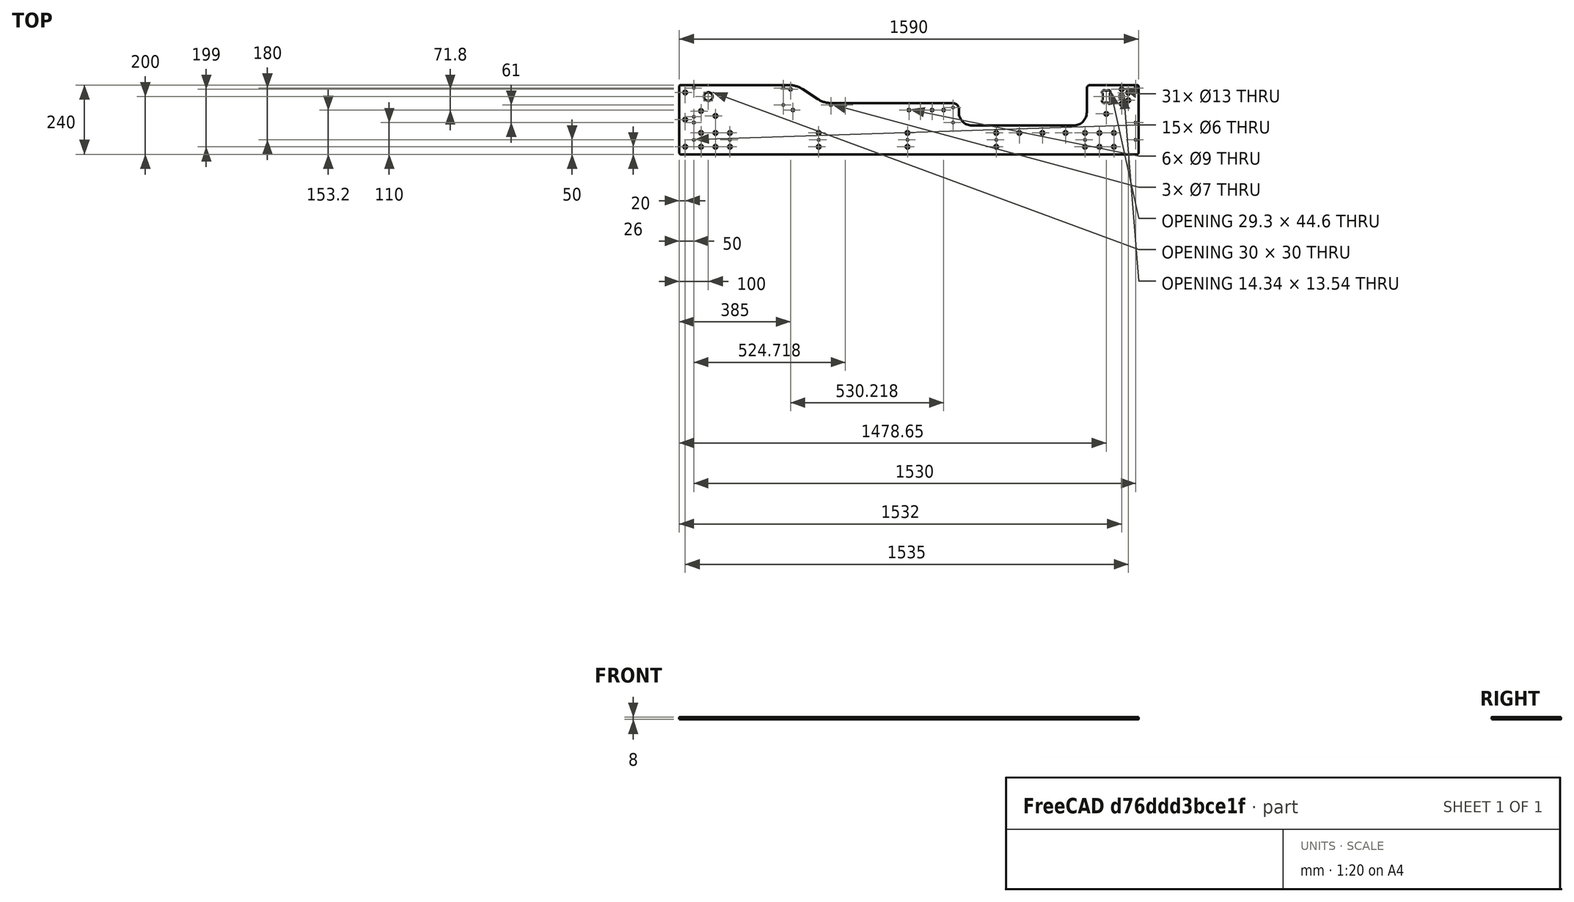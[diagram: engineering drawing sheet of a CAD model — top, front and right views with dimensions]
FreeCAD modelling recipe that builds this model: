
FCSTD DOCUMENT  (FreeCAD 0.19R24267 +99 (Git))
Label: V2 Side mounting plate
License: All rights reserved
LicenseURL: http://en.wikipedia.org/wiki/All_rights_reserved
objects: Sketcher::SketchObject×1, PartDesign::Pad×1, PartDesign::Body×1
note: 4 computed .brp shape members not serialized (recipe doc carries the construction recipe); baked Part::Feature solids carry a one-line shape summary decoded from their .brp

FEATURE [Sketcher::SketchObject] Sketch  label="Profile and holes sketch"
  FullyConstrained = true
  MapMode = 5
  Support = -> [XY_Plane]
  sketch-geometry (196):
    g0: LineSegment StartX=750 StartY=140 StartZ=0 EndX=750 EndY=-100 EndZ=0
    g1: LineSegment StartX=-750 StartY=-100 StartZ=0 EndX=-750 EndY=140 EndZ=0
    g2: ArcOfCircle CenterX=-690 CenterY=100 CenterZ=0 NormalX=0 NormalY=0 NormalZ=1 AngleXU=0 Radius=15 StartAngle=4.71239 EndAngle=7.85398
    g3: LineSegment StartX=223 StartY=0 StartZ=0 EndX=576 EndY=0 EndZ=0
    g4: LineSegment StartX=621 StartY=45 StartZ=0 EndX=621 EndY=128 EndZ=0
    g5: LineSegment StartX=-690 StartY=100 StartZ=0 EndX=60.218 EndY=100 EndZ=0
    g6: LineSegment StartX=60.218 StartY=100 StartZ=0 EndX=60.218 EndY=53.2 EndZ=0
    g7: LineSegment StartX=178 StartY=53.2 StartZ=0 EndX=-750 EndY=53.2 EndZ=0
    g8: LineSegment StartX=-307.5 StartY=-26 StartZ=0 EndX=-307.5 EndY=-74 EndZ=0
    g9: LineSegment StartX=307.5 StartY=-26 StartZ=0 EndX=307.5 EndY=-74 EndZ=0
    g10: LineSegment StartX=715 StartY=-26 StartZ=0 EndX=715 EndY=-74 EndZ=0
    g11: LineSegment StartX=-307.5 StartY=-74 StartZ=0 EndX=0 EndY=-74 EndZ=0
    g12: LineSegment StartX=2.29e-14 StartY=-74 StartZ=0 EndX=307.5 EndY=-74 EndZ=0
    g13: GeomPoint X=2.29e-14 Y=-26 Z=0
    g14: Circle CenterX=-715 CenterY=50 CenterZ=0 NormalX=0 NormalY=0 NormalZ=1 AngleXU=0 Radius=6.5
    g15: Circle CenterX=-665 CenterY=33 CenterZ=0 NormalX=0 NormalY=0 NormalZ=1 AngleXU=0 Radius=6.5
    g16: Circle CenterX=-715 CenterY=-26 CenterZ=0 NormalX=0 NormalY=0 NormalZ=1 AngleXU=0 Radius=6.5
    g17: Circle CenterX=-307.5 CenterY=-26 CenterZ=0 NormalX=0 NormalY=0 NormalZ=1 AngleXU=0 Radius=6.5
    g18: Circle CenterX=-307.5 CenterY=-74 CenterZ=0 NormalX=0 NormalY=0 NormalZ=1 AngleXU=0 Radius=6.5
    g19: Circle CenterX=2.29e-14 CenterY=-74 CenterZ=0 NormalX=0 NormalY=0 NormalZ=1 AngleXU=0 Radius=6.5
    g20: Circle CenterX=2.29e-14 CenterY=-26 CenterZ=0 NormalX=0 NormalY=0 NormalZ=1 AngleXU=0 Radius=6.5
    g21: Circle CenterX=307.5 CenterY=-74 CenterZ=0 NormalX=0 NormalY=0 NormalZ=1 AngleXU=0 Radius=6.5
    g22: Circle CenterX=307.5 CenterY=-26 CenterZ=0 NormalX=0 NormalY=0 NormalZ=1 AngleXU=0 Radius=6.5
    g23: Circle CenterX=715 CenterY=-26 CenterZ=0 NormalX=0 NormalY=0 NormalZ=1 AngleXU=0 Radius=6.5
    g24: Circle CenterX=715 CenterY=-74 CenterZ=0 NormalX=0 NormalY=0 NormalZ=1 AngleXU=0 Radius=6.5
    g25: Circle CenterX=307.5 CenterY=-50 CenterZ=0 NormalX=0 NormalY=0 NormalZ=1 AngleXU=0 Radius=3
    g26: Circle CenterX=-307.5 CenterY=-50 CenterZ=0 NormalX=0 NormalY=0 NormalZ=1 AngleXU=0 Radius=3
    g27: LineSegment StartX=-786 StartY=140 StartZ=0 EndX=-412 EndY=140 EndZ=0
    g28: LineSegment StartX=-362.763 StartY=125.338 StartZ=0 EndX=-311.237 EndY=91.6625 EndZ=0
    g29: LineSegment StartX=-262 StartY=77 StartZ=0 EndX=158 EndY=77 EndZ=0
    g30: ArcOfCircle CenterX=-412 CenterY=50 CenterZ=0 NormalX=0 NormalY=0 NormalZ=1 AngleXU=0 Radius=90 StartAngle=0.991931 EndAngle=1.5708
    g31: ArcOfCircle CenterX=-262 CenterY=167 CenterZ=0 NormalX=0 NormalY=0 NormalZ=1 AngleXU=0 Radius=90 StartAngle=4.13352 EndAngle=4.71239
    g32: LineSegment StartX=633 StartY=140 StartZ=0 EndX=796 EndY=140 EndZ=0
    g33: ArcOfCircle CenterX=158 CenterY=57 CenterZ=0 NormalX=0 NormalY=0 NormalZ=1 AngleXU=0 Radius=20 StartAngle=0 EndAngle=1.5708
    g34: LineSegment StartX=-715 StartY=-26 StartZ=0 EndX=-715 EndY=-74 EndZ=0
    g35: Circle CenterX=-715 CenterY=-74 CenterZ=0 NormalX=0 NormalY=0 NormalZ=1 AngleXU=0 Radius=6.5
    g36: LineSegment StartX=688.244 StartY=120.3 StartZ=0 EndX=689.056 EndY=120.3 EndZ=0
    g37: LineSegment StartX=701.3 StartY=108.056 StartZ=0 EndX=701.3 EndY=91.9438 EndZ=0
    g38: LineSegment StartX=689.056 StartY=79.7 StartZ=0 EndX=688.244 EndY=79.7 EndZ=0
    g39: LineSegment StartX=676 StartY=91.9438 StartZ=0 EndX=676 EndY=108.056 EndZ=0
    g40: ArcOfCircle CenterX=680.95 CenterY=115.35 CenterZ=0 NormalX=0 NormalY=0 NormalZ=1 AngleXU=0 Radius=7 StartAngle=1.02277 EndAngle=3.68962
    g41: ArcOfCircle CenterX=680.95 CenterY=84.6497 CenterZ=0 NormalX=0 NormalY=0 NormalZ=1 AngleXU=0 Radius=7 StartAngle=2.59356 EndAngle=5.26042
    g42: ArcOfCircle CenterX=696.35 CenterY=84.6497 CenterZ=0 NormalX=0 NormalY=0 NormalZ=1 AngleXU=0 Radius=7 StartAngle=4.16436 EndAngle=6.83121
    g43: ArcOfCircle CenterX=696.35 CenterY=115.35 CenterZ=0 NormalX=0 NormalY=0 NormalZ=1 AngleXU=0 Radius=7 StartAngle=5.73516 EndAngle=8.40201
    g44: LineSegment StartX=676 StartY=108.056 StartZ=0 EndX=676 EndY=120.3 EndZ=0
    g45: LineSegment StartX=688.244 StartY=120.3 StartZ=0 EndX=676 EndY=120.3 EndZ=0
    g46: LineSegment StartX=689.056 StartY=120.3 StartZ=0 EndX=701.3 EndY=120.3 EndZ=0
    g47: LineSegment StartX=701.3 StartY=108.056 StartZ=0 EndX=701.3 EndY=120.3 EndZ=0
    g48: LineSegment StartX=688.244 StartY=79.7 StartZ=0 EndX=676 EndY=79.7 EndZ=0
    g49: LineSegment StartX=676 StartY=91.9438 StartZ=0 EndX=676 EndY=79.7 EndZ=0
    g50: LineSegment StartX=689.056 StartY=79.7 StartZ=0 EndX=701.3 EndY=79.7 EndZ=0
    g51: LineSegment StartX=701.3 StartY=91.9438 StartZ=0 EndX=701.3 EndY=79.7 EndZ=0
    g52: ArcOfCircle CenterX=669 CenterY=108.056 CenterZ=0 NormalX=0 NormalY=0 NormalZ=1 AngleXU=0 Radius=7 StartAngle=0 EndAngle=0.548028
    g53: ArcOfCircle CenterX=688.244 CenterY=127.3 CenterZ=0 NormalX=0 NormalY=0 NormalZ=1 AngleXU=0 Radius=7 StartAngle=4.16436 EndAngle=4.71239
    g54: ArcOfCircle CenterX=689.056 CenterY=127.3 CenterZ=0 NormalX=0 NormalY=0 NormalZ=1 AngleXU=0 Radius=7 StartAngle=4.71239 EndAngle=5.26042
    g55: ArcOfCircle CenterX=708.3 CenterY=108.056 CenterZ=0 NormalX=0 NormalY=0 NormalZ=1 AngleXU=0 Radius=7 StartAngle=2.59356 EndAngle=3.14159
    g56: ArcOfCircle CenterX=708.3 CenterY=91.9438 CenterZ=0 NormalX=0 NormalY=0 NormalZ=1 AngleXU=0 Radius=7 StartAngle=3.14159 EndAngle=3.68962
    g57: ArcOfCircle CenterX=689.056 CenterY=72.7 CenterZ=0 NormalX=0 NormalY=0 NormalZ=1 AngleXU=0 Radius=7 StartAngle=1.02277 EndAngle=1.5708
    g58: ArcOfCircle CenterX=688.244 CenterY=72.7 CenterZ=0 NormalX=0 NormalY=0 NormalZ=1 AngleXU=0 Radius=7 StartAngle=1.5708 EndAngle=2.11882
    g59: ArcOfCircle CenterX=669 CenterY=91.9438 CenterZ=0 NormalX=0 NormalY=0 NormalZ=1 AngleXU=0 Radius=7 StartAngle=5.73516 EndAngle=6.28319
    g60: LineSegment StartX=60.218 StartY=100 StartZ=0 EndX=800 EndY=100 EndZ=0
    g61: LineSegment StartX=800 StartY=-96 StartZ=0 EndX=800 EndY=136 EndZ=0
    g62: ArcOfCircle CenterX=796 CenterY=-96 CenterZ=0 NormalX=0 NormalY=0 NormalZ=1 AngleXU=0 Radius=4 StartAngle=4.71239 EndAngle=6.28319
    g63: LineSegment StartX=-430 StartY=71 StartZ=0 EndX=-430 EndY=130 EndZ=0
    g64: Circle CenterX=-430 CenterY=130 CenterZ=0 NormalX=0 NormalY=0 NormalZ=1 AngleXU=0 Radius=3
    g65: Circle CenterX=-430 CenterY=71 CenterZ=0 NormalX=0 NormalY=0 NormalZ=1 AngleXU=0 Radius=3
    g66: LineSegment StartX=665 StartY=-74 StartZ=0 EndX=665 EndY=-26 EndZ=0
    g67: LineSegment StartX=615 StartY=-74 StartZ=0 EndX=615 EndY=-26 EndZ=0
    g68: Circle CenterX=615 CenterY=-26 CenterZ=0 NormalX=0 NormalY=0 NormalZ=1 AngleXU=0 Radius=6.5
    g69: Circle CenterX=665 CenterY=-26 CenterZ=0 NormalX=0 NormalY=0 NormalZ=1 AngleXU=0 Radius=6.5
    g70: Circle CenterX=615 CenterY=-74 CenterZ=0 NormalX=0 NormalY=0 NormalZ=1 AngleXU=0 Radius=6.5
    g71: Circle CenterX=665 CenterY=-74 CenterZ=0 NormalX=0 NormalY=0 NormalZ=1 AngleXU=0 Radius=6.5
    g72: ArcOfCircle CenterX=796 CenterY=136 CenterZ=0 NormalX=0 NormalY=0 NormalZ=1 AngleXU=0 Radius=4 StartAngle=2.1e-15 EndAngle=1.5708
    g73: LineSegment StartX=2.29e-14 StartY=-26 StartZ=0 EndX=2.29e-14 EndY=-74 EndZ=0
    g74: Circle CenterX=2.29e-14 CenterY=-50 CenterZ=0 NormalX=0 NormalY=0 NormalZ=1 AngleXU=0 Radius=3
    g75: LineSegment StartX=576 StartY=0 StartZ=0 EndX=750 EndY=0 EndZ=0
    g76: LineSegment StartX=750 StartY=-50 StartZ=0 EndX=800 EndY=-50 EndZ=0
    g77: Circle CenterX=790 CenterY=-50 CenterZ=0 NormalX=0 NormalY=0 NormalZ=1 AngleXU=0 Radius=3
    g78: ArcOfCircle CenterX=576 CenterY=45 CenterZ=0 NormalX=0 NormalY=0 NormalZ=1 AngleXU=0 Radius=45 StartAngle=4.71239 EndAngle=6.28319
    g79: LineSegment StartX=742 StartY=125 StartZ=0 EndX=742 EndY=75 EndZ=0
    g80: LineSegment StartX=765 StartY=113 StartZ=0 EndX=765 EndY=87 EndZ=0
    g81: Circle CenterX=742 CenterY=125 CenterZ=0 NormalX=0 NormalY=0 NormalZ=1 AngleXU=0 Radius=6.5
    g82: Circle CenterX=765 CenterY=113 CenterZ=0 NormalX=0 NormalY=0 NormalZ=1 AngleXU=0 Radius=6.5
    g83: Circle CenterX=765 CenterY=87 CenterZ=0 NormalX=0 NormalY=0 NormalZ=1 AngleXU=0 Radius=6.5
    g84: Circle CenterX=742 CenterY=75 CenterZ=0 NormalX=0 NormalY=0 NormalZ=1 AngleXU=0 Radius=6.5
    g85: LineSegment StartX=796 StartY=-100 StartZ=0 EndX=-786 EndY=-100 EndZ=0
    g86: LineSegment StartX=-665 StartY=-74 StartZ=0 EndX=-665 EndY=-26 EndZ=0
    g87: LineSegment StartX=-615 StartY=-74 StartZ=0 EndX=-615 EndY=-26 EndZ=0
    g88: Circle CenterX=-665 CenterY=-74 CenterZ=0 NormalX=0 NormalY=0 NormalZ=1 AngleXU=0 Radius=6.5
    g89: Circle CenterX=-615 CenterY=-74 CenterZ=0 NormalX=0 NormalY=0 NormalZ=1 AngleXU=0 Radius=6.5
    g90: Circle CenterX=-665 CenterY=-26 CenterZ=0 NormalX=0 NormalY=0 NormalZ=1 AngleXU=0 Radius=6.5
    g91: Circle CenterX=-615 CenterY=-26 CenterZ=0 NormalX=0 NormalY=0 NormalZ=1 AngleXU=0 Radius=6.5
    g92: LineSegment StartX=-715 StartY=-74 StartZ=0 EndX=-665 EndY=-74 EndZ=0
    g93: LineSegment StartX=-665 StartY=-74 StartZ=0 EndX=-615 EndY=-74 EndZ=0
    g94: LineSegment StartX=-615 StartY=-74 StartZ=0 EndX=-307.5 EndY=-74 EndZ=0
    g95: LineSegment StartX=307.5 StartY=-74 StartZ=0 EndX=615 EndY=-74 EndZ=0
    g96: LineSegment StartX=615 StartY=-74 StartZ=0 EndX=665 EndY=-74 EndZ=0
    g97: LineSegment StartX=665 StartY=-74 StartZ=0 EndX=715 EndY=-74 EndZ=0
    g98: Circle CenterX=-396.782 CenterY=53.2 CenterZ=0 NormalX=0 NormalY=0 NormalZ=1 AngleXU=0 Radius=4.5
    g99: Circle CenterX=5.218 CenterY=53.2 CenterZ=0 NormalX=0 NormalY=0 NormalZ=1 AngleXU=0 Radius=4.5
    g100: Circle CenterX=45.218 CenterY=53.2 CenterZ=0 NormalX=0 NormalY=0 NormalZ=1 AngleXU=0 Radius=4.5
    g101: Circle CenterX=85.218 CenterY=53.2 CenterZ=0 NormalX=0 NormalY=0 NormalZ=1 AngleXU=0 Radius=4.5
    g102: Circle CenterX=125.218 CenterY=53.2 CenterZ=0 NormalX=0 NormalY=0 NormalZ=1 AngleXU=0 Radius=4.5
    g103: LineSegment StartX=-715 StartY=-50 StartZ=0 EndX=-665 EndY=-50 EndZ=0
    g104: LineSegment StartX=-665 StartY=-50 StartZ=0 EndX=-615 EndY=-50 EndZ=0
    g105: LineSegment StartX=-615 StartY=-50 StartZ=0 EndX=-307.5 EndY=-50 EndZ=0
    g106: LineSegment StartX=-307.5 StartY=-50 StartZ=0 EndX=0 EndY=-50 EndZ=0
    g107: LineSegment StartX=2.29e-14 StartY=-50 StartZ=0 EndX=307.5 EndY=-50 EndZ=0
    g108: LineSegment StartX=307.5 StartY=-50 StartZ=0 EndX=615 EndY=-50 EndZ=0
    g109: LineSegment StartX=615 StartY=-50 StartZ=0 EndX=665 EndY=-50 EndZ=0
    g110: LineSegment StartX=665 StartY=-50 StartZ=0 EndX=715 EndY=-50 EndZ=0
    g111: LineSegment StartX=738.898 StartY=106.2 StartZ=0 EndX=745.102 EndY=106.2 EndZ=0
    g112: LineSegment StartX=748.6 StartY=102.702 StartZ=0 EndX=748.6 EndY=97.2982 EndZ=0
    g113: LineSegment StartX=745.102 StartY=93.8 StartZ=0 EndX=738.898 EndY=93.8 EndZ=0
    g114: LineSegment StartX=735.4 StartY=97.2982 StartZ=0 EndX=735.4 EndY=102.702 EndZ=0
    g115: ArcOfCircle CenterX=736.814 CenterY=104.786 CenterZ=0 NormalX=0 NormalY=0 NormalZ=1 AngleXU=0 Radius=2 StartAngle=1.02277 EndAngle=3.68962
    g116: ArcOfCircle CenterX=747.186 CenterY=95.2142 CenterZ=0 NormalX=0 NormalY=0 NormalZ=1 AngleXU=0 Radius=2 StartAngle=4.16436 EndAngle=6.83121
    g117: LineSegment StartX=735.4 StartY=97.2982 StartZ=0 EndX=735.4 EndY=93.8 EndZ=0
    g118: LineSegment StartX=745.102 StartY=93.8 StartZ=0 EndX=748.6 EndY=93.8 EndZ=0
    g119: LineSegment StartX=748.6 StartY=102.702 StartZ=0 EndX=748.6 EndY=106.2 EndZ=0
    g120: LineSegment StartX=738.898 StartY=106.2 StartZ=0 EndX=735.4 EndY=106.2 EndZ=0
    g121: LineSegment StartX=735.4 StartY=102.702 StartZ=0 EndX=735.4 EndY=106.2 EndZ=0
    g122: LineSegment StartX=738.898 StartY=93.8 StartZ=0 EndX=735.4 EndY=93.8 EndZ=0
    g123: LineSegment StartX=748.6 StartY=97.2982 StartZ=0 EndX=748.6 EndY=93.8 EndZ=0
    g124: LineSegment StartX=745.102 StartY=106.2 StartZ=0 EndX=748.6 EndY=106.2 EndZ=0
    g125: ArcOfCircle CenterX=733.4 CenterY=102.702 CenterZ=0 NormalX=0 NormalY=0 NormalZ=1 AngleXU=0 Radius=2 StartAngle=1e-15 EndAngle=0.548028
    g126: ArcOfCircle CenterX=738.898 CenterY=108.2 CenterZ=0 NormalX=0 NormalY=0 NormalZ=1 AngleXU=0 Radius=2 StartAngle=4.16436 EndAngle=4.71239
    g127: ArcOfCircle CenterX=745.102 CenterY=91.8 CenterZ=0 NormalX=0 NormalY=0 NormalZ=1 AngleXU=0 Radius=2 StartAngle=1.02277 EndAngle=1.5708
    g128: ArcOfCircle CenterX=750.6 CenterY=97.2982 CenterZ=0 NormalX=0 NormalY=0 NormalZ=1 AngleXU=0 Radius=2 StartAngle=3.14159 EndAngle=3.68962
    g129: ArcOfCircle CenterX=747.186 CenterY=104.786 CenterZ=0 NormalX=0 NormalY=0 NormalZ=1 AngleXU=0 Radius=2 StartAngle=5.73516 EndAngle=8.40201
    g130: ArcOfCircle CenterX=745.102 CenterY=108.2 CenterZ=0 NormalX=0 NormalY=0 NormalZ=1 AngleXU=0 Radius=2 StartAngle=4.71239 EndAngle=5.26042
    g131: ArcOfCircle CenterX=750.6 CenterY=102.702 CenterZ=0 NormalX=0 NormalY=0 NormalZ=1 AngleXU=0 Radius=2 StartAngle=2.59356 EndAngle=3.14159
    g132: ArcOfCircle CenterX=736.814 CenterY=95.2142 CenterZ=0 NormalX=0 NormalY=0 NormalZ=1 AngleXU=0 Radius=2 StartAngle=2.59356 EndAngle=5.26042
    g133: ArcOfCircle CenterX=733.4 CenterY=97.2982 CenterZ=0 NormalX=0 NormalY=0 NormalZ=1 AngleXU=0 Radius=2 StartAngle=5.73516 EndAngle=6.28319
    g134: ArcOfCircle CenterX=738.898 CenterY=91.8 CenterZ=0 NormalX=0 NormalY=0 NormalZ=1 AngleXU=0 Radius=2 StartAngle=1.5708 EndAngle=2.11882
    g135: GeomPoint X=742 Y=100 Z=0
    g136: LineSegment StartX=-715 StartY=-50 StartZ=0 EndX=-750 EndY=-50 EndZ=0
    g137: LineSegment StartX=715 StartY=-50 StartZ=0 EndX=750 EndY=-50 EndZ=0
    g138: LineSegment StartX=780 StartY=-50 StartZ=0 EndX=780 EndY=140 EndZ=0
    g139: LineSegment StartX=-412 StartY=140 StartZ=0 EndX=633 EndY=140 EndZ=0
    g140: Circle CenterX=60.218 CenterY=100 CenterZ=0 NormalX=0 NormalY=0 NormalZ=1 AngleXU=0 Radius=15
    g141: GeomPoint X=790 Y=10 Z=0
    g142: GeomPoint X=790 Y=130 Z=0
    g143: LineSegment StartX=780 StartY=-40 StartZ=0 EndX=800 EndY=-40 EndZ=0
    g144: Circle CenterX=790 CenterY=10 CenterZ=0 NormalX=0 NormalY=0 NormalZ=1 AngleXU=0 Radius=3
    g145: Circle CenterX=790 CenterY=130 CenterZ=0 NormalX=0 NormalY=0 NormalZ=1 AngleXU=0 Radius=3
    g146: LineSegment StartX=790 StartY=10 StartZ=0 EndX=790 EndY=-40 EndZ=0
    g147: LineSegment StartX=790 StartY=10 StartZ=0 EndX=790 EndY=130 EndZ=0
    g148: LineSegment StartX=790 StartY=130 StartZ=0 EndX=790 EndY=140 EndZ=0
    g149: LineSegment StartX=-730 StartY=140 StartZ=0 EndX=-730 EndY=-40 EndZ=0
    g150: LineSegment StartX=-730 StartY=-40 StartZ=0 EndX=-750 EndY=-40 EndZ=0
    g151: Circle CenterX=-740 CenterY=-50 CenterZ=0 NormalX=0 NormalY=0 NormalZ=1 AngleXU=0 Radius=3
    g152: LineSegment StartX=-740 StartY=-40 StartZ=0 EndX=-740 EndY=10 EndZ=0
    g153: LineSegment StartX=-740 StartY=10 StartZ=0 EndX=-740 EndY=130 EndZ=0
    g154: LineSegment StartX=-740 StartY=130 StartZ=0 EndX=-740 EndY=140 EndZ=0
    g155: Circle CenterX=-740 CenterY=10 CenterZ=0 NormalX=0 NormalY=0 NormalZ=1 AngleXU=0 Radius=3.5
    g156: Circle CenterX=-740 CenterY=130 CenterZ=0 NormalX=0 NormalY=0 NormalZ=1 AngleXU=0 Radius=3
    g157: Circle CenterX=387.5 CenterY=-26 CenterZ=0 NormalX=0 NormalY=0 NormalZ=1 AngleXU=0 Radius=6.5
    g158: Circle CenterX=467.5 CenterY=-26 CenterZ=0 NormalX=0 NormalY=0 NormalZ=1 AngleXU=0 Radius=6.5
    g159: Circle CenterX=547.5 CenterY=-26 CenterZ=0 NormalX=0 NormalY=0 NormalZ=1 AngleXU=0 Radius=6.5
    g160: LineSegment StartX=387.5 StartY=-26 StartZ=0 EndX=387.5 EndY=-74 EndZ=0
    g161: LineSegment StartX=467.5 StartY=-26 StartZ=0 EndX=467.5 EndY=-74 EndZ=0
    g162: LineSegment StartX=547.5 StartY=-26 StartZ=0 EndX=547.5 EndY=-74 EndZ=0
    g163: Circle CenterX=158 CenterY=62 CenterZ=0 NormalX=0 NormalY=0 NormalZ=1 AngleXU=0 Radius=3
    g164: LineSegment StartX=158 StartY=62 StartZ=0 EndX=158 EndY=10 EndZ=0
    g165: Circle CenterX=158 CenterY=10 CenterZ=0 NormalX=0 NormalY=0 NormalZ=1 AngleXU=0 Radius=3
    g166: LineSegment StartX=-790 StartY=136 StartZ=0 EndX=-790 EndY=-96 EndZ=0
    g167: ArcOfCircle CenterX=-786 CenterY=136 CenterZ=0 NormalX=0 NormalY=0 NormalZ=1 AngleXU=0 Radius=4 StartAngle=1.5708 EndAngle=3.14159
    g168: ArcOfCircle CenterX=-786 CenterY=-96 CenterZ=0 NormalX=0 NormalY=0 NormalZ=1 AngleXU=0 Radius=4 StartAngle=3.14159 EndAngle=4.71239
    g169: Circle CenterX=-770 CenterY=-74 CenterZ=0 NormalX=0 NormalY=0 NormalZ=1 AngleXU=0 Radius=6.5
    g170: Circle CenterX=-770 CenterY=114 CenterZ=0 NormalX=0 NormalY=0 NormalZ=1 AngleXU=0 Radius=6.5
    g171: ArcOfCircle CenterX=633 CenterY=128 CenterZ=0 NormalX=0 NormalY=0 NormalZ=1 AngleXU=0 Radius=12 StartAngle=1.5708 EndAngle=3.14159
    g172: Circle CenterX=-740 CenterY=30 CenterZ=0 NormalX=0 NormalY=0 NormalZ=1 AngleXU=0 Radius=3
    g173: Circle CenterX=-770 CenterY=20 CenterZ=0 NormalX=0 NormalY=0 NormalZ=1 AngleXU=0 Radius=6.5
    g174: LineSegment StartX=-770 StartY=-74 StartZ=0 EndX=-770 EndY=-100 EndZ=0
    g175: LineSegment StartX=-770 StartY=-74 StartZ=0 EndX=-770 EndY=20 EndZ=0
    g176: LineSegment StartX=-770 StartY=20 StartZ=0 EndX=-770 EndY=114 EndZ=0
    g177: LineSegment StartX=-770 StartY=114 StartZ=0 EndX=-770 EndY=140 EndZ=0
    g178: LineSegment StartX=-715 StartY=-74 StartZ=0 EndX=-770 EndY=-74 EndZ=0
    g179: Circle CenterX=-405 CenterY=125 CenterZ=0 NormalX=0 NormalY=0 NormalZ=1 AngleXU=0 Radius=4.5
    g180: Circle CenterX=688.8 CenterY=30 CenterZ=0 NormalX=0 NormalY=0 NormalZ=1 AngleXU=0 Radius=6.5
    g181: LineSegment StartX=178 StartY=57 StartZ=0 EndX=178 EndY=45 EndZ=0
    g182: ArcOfCircle CenterX=223 CenterY=45 CenterZ=0 NormalX=0 NormalY=0 NormalZ=1 AngleXU=0 Radius=45 StartAngle=3.14159 EndAngle=4.71239
    g183: GeomPoint X=320 Y=-50 Z=0
    g184: LineSegment StartX=-690 StartY=100 StartZ=0 EndX=-690 EndY=115 EndZ=0
    g185: LineSegment StartX=-690 StartY=100 StartZ=0 EndX=-690 EndY=85 EndZ=0
    g186: ArcOfCircle CenterX=-690 CenterY=100 CenterZ=0 NormalX=0 NormalY=0 NormalZ=1 AngleXU=0 Radius=15 StartAngle=1.5708 EndAngle=4.71239
    g187: LineSegment StartX=-215.282 StartY=71 StartZ=0 EndX=-265.282 EndY=71 EndZ=0
    g188: Circle CenterX=-265.282 CenterY=71 CenterZ=0 NormalX=0 NormalY=0 NormalZ=1 AngleXU=0 Radius=3.5
    g189: Circle CenterX=-215.282 CenterY=71 CenterZ=0 NormalX=0 NormalY=0 NormalZ=1 AngleXU=0 Radius=3.5
    g190: GeomPoint X=-240.282 Y=71 Z=0
    g191: Circle CenterX=615 CenterY=-50 CenterZ=0 NormalX=0 NormalY=0 NormalZ=1 AngleXU=0 Radius=3
    g192: Circle CenterX=-615 CenterY=-50 CenterZ=0 NormalX=0 NormalY=0 NormalZ=1 AngleXU=0 Radius=3
    g193: Circle CenterX=-690 CenterY=100 CenterZ=0 NormalX=0 NormalY=0 NormalZ=1 AngleXU=0 Radius=6.5
    g194: LineSegment StartX=-265.282 StartY=71 StartZ=0 EndX=-430 EndY=71 EndZ=0
    g195: Circle CenterX=60.218 CenterY=100 CenterZ=0 NormalX=0 NormalY=0 NormalZ=1 AngleXU=0 Radius=22.5
  constraints (526):
    c: Vertical(g0)
    c: Vertical(g1)
    c: DistanceY(g-1,g2) = 100
    c: DistanceX(g1,g2) = 60
    c: Horizontal(g3)
    c: PointOnObject(g-1,g3)
    c: Coincident(g5,g2)
    c: Horizontal(g5)
    c: DistanceX(g5,g5) = 750.218
    c: Vertical(g6)
    c: DistanceY(g-1,g6) = 53.2
    c: Horizontal(g7)
    c: PointOnObject(g7,g1)
    c: PointOnObject(g6,g7)
    c: DistanceX(g1,g0) = 1500
    c: Coincident(g11,g8)
    c: Horizontal(g11)
    c: Coincident(g12,g9)
    c: Horizontal(g12)
    c: DistanceX(g14,g2) = 25
    c: DistanceX(g2,g15) = 25
    c: Equal(g14,g15)
    c: DistanceY(g15,g14) = 17
    c: DistanceY(g-1,g15) = 33
    c: Coincident(g17,g8)
    c: Coincident(g18,g8)
    c: Coincident(g20,g13)
    c: Coincident(g21,g9)
    c: Coincident(g22,g9)
    c: Coincident(g23,g10)
    c: Coincident(g24,g10)
    c: Equal(g24,g23)
    c: Equal(g21,g22)
    c: Equal(g22,g19)
    c: Equal(g19,g20)
    c: Equal(g18,g17)
    c: Coincident(g5,g6)
    c: Horizontal(g27)
    c: Horizontal(g29)
    c: Tangent(g28,g30) = 1.5708
    c: Tangent(g27,g30) = 1.5708
    c: Tangent(g28,g31) = -1.5708
    c: Tangent(g29,g31) = -1.5708
    c: DistanceY(g-1,g29) = 77
    c: DistanceX(g27,g29) = 150
    c: Equal(g30,g31)
    c: Radius(g30) = 90
    c: Horizontal(g32)
    c: Tangent(g33,g29) = 1.5708
    c: Coincident(g34,g16)
    c: Equal(g35,g16)
    c: Equal(g17,g16)
    c: Horizontal(g36)
    c: Horizontal(g38)
    c: Vertical(g37)
    c: Vertical(g39)
    c: PointOnObject(g44,g40)
    c: Coincident(g45,g44)
    c: PointOnObject(g46,g43)
    c: Coincident(g47,g46)
    c: PointOnObject(g48,g41)
    c: Coincident(g49,g48)
    c: PointOnObject(g50,g42)
    c: Coincident(g51,g50)
    c: Equal(g41,g40)
    c: Equal(g40,g43)
    c: Equal(g43,g42)
    c: Equal(g49,g48)
    c: Equal(g48,g50)
    c: Equal(g50,g51)
    c: Equal(g51,g47)
    c: Equal(g47,g46)
    c: Equal(g46,g45)
    c: Equal(g45,g44)
    c: Vertical(g44)
    c: Vertical(g49)
    c: Vertical(g51)
    c: Vertical(g47)
    c: Horizontal(g45)
    c: Tangent(g40,g52) = 1.5708
    c: Tangent(g39,g52) = -1.5708
    c: Tangent(g40,g53) = 1.5708
    c: Tangent(g36,g53) = -1.5708
    c: Tangent(g43,g54) = 1.5708
    c: Tangent(g36,g54) = -1.5708
    c: Tangent(g43,g55) = 1.5708
    c: Tangent(g37,g55) = -1.5708
    c: Tangent(g42,g56) = 1.5708
    c: Tangent(g37,g56) = -1.5708
    c: Tangent(g38,g57) = -1.5708
    c: Tangent(g42,g57) = 1.5708
    c: Tangent(g41,g58) = 1.5708
    c: Tangent(g38,g58) = -1.5708
    c: Tangent(g41,g59) = 1.5708
    c: Tangent(g39,g59) = -1.5708
    c: Coincident(g39,g49)
    c: Coincident(g38,g48)
    c: Coincident(g39,g44)
    c: Coincident(g36,g45)
    c: Coincident(g36,g46)
    c: Coincident(g37,g47)
    c: Coincident(g38,g50)
    c: Coincident(g37,g51)
    c: Horizontal(g48)
    c: Horizontal(g50)
    c: DistanceY(g50,g46) = 40.6
    c: Equal(g40,g53)
    c: Equal(g53,g52)
    c: Equal(g52,g59)
    c: Equal(g40,g54)
    c: Equal(g54,g55)
    c: Equal(g55,g56)
    c: Radius(g40) = 7
    c: Coincident(g60,g5)
    c: Symmetric(g44,g48,g60)
    c: DistanceX(g29,g29) = 420
    c: Vertical(g61)
    c: Tangent(g61,g62) = -1.5708
    c: DistanceX(g0,g61) = 50
    c: Vertical(g63)
    c: Coincident(g64,g63)
    c: Equal(g65,g64)
    c: DistanceY(g35,g16) = 48
    c: Coincident(g68,g67)
    c: Coincident(g69,g66)
    c: Coincident(g70,g67)
    c: Coincident(g71,g66)
    c: Equal(g71,g70)
    c: Equal(g70,g68)
    c: Equal(g68,g69)
    c: Equal(g69,g16)
    c: PointOnObject(g0,g32)
    c: Tangent(g61,g72) = -1.5708
    c: Tangent(g32,g72) = 1.5708
    c: Coincident(g73,g20)
    c: Coincident(g73,g19)
    c: Vertical(g73)
    c: Vertical(g34)
    c: PointOnObject(g76,g0)
    c: PointOnObject(g75,g0)
    c: Horizontal(g75)
    c: DistanceY(g0,g75) = 100
    c: PointOnObject(g76,g61)
    c: PointOnObject(g77,g76)
    c: DistanceX(g77,g76) = 10
    c: Vertical(g4)
    c: Tangent(g4,g78) = -1.5708
    c: Tangent(g3,g78) = -1.5708
    c: Coincident(g75,g3)
    c: Radius(g78) = 45
    c: PointOnObject(g60,g61)
    c: Symmetric(g79,g79,g60)
    c: Symmetric(g80,g80,g60)
    c: Coincident(g81,g79)
    c: Coincident(g82,g80)
    c: Coincident(g83,g80)
    c: Coincident(g84,g79)
    c: Equal(g84,g81)
    c: Equal(g81,g82)
    c: Equal(g82,g83)
    c: DistanceY(g80,g80) = 26
    c: Distance(g80,g79) = 25.9422
    c: DistanceY(g79,g79) = 50
    c: Coincident(g65,g63)
    c: Horizontal(g85)
    c: PointOnObject(g0,g85)
    c: Tangent(g85,g62) = 1.5708
    c: Equal(g72,g62)
    c: DistanceY(g60,g32) = 40
    c: Coincident(g88,g86)
    c: Coincident(g89,g87)
    c: Coincident(g90,g86)
    c: Coincident(g91,g87)
    c: Equal(g16,g90)
    c: Equal(g90,g88)
    c: Equal(g88,g89)
    c: Equal(g89,g91)
    c: Coincident(g19,g11)
    c: Coincident(g19,g12)
    c: Coincident(g34,g35)
    c: Coincident(g92,g35)
    c: Coincident(g92,g88)
    c: Horizontal(g92)
    c: Coincident(g93,g88)
    c: Coincident(g93,g89)
    c: Horizontal(g93)
    c: Coincident(g94,g89)
    c: Coincident(g94,g18)
    c: Horizontal(g94)
    c: Coincident(g95,g21)
    c: Coincident(g95,g70)
    c: Horizontal(g95)
    c: Coincident(g96,g70)
    c: Coincident(g96,g71)
    c: Horizontal(g96)
    c: Coincident(g97,g71)
    c: Coincident(g97,g24)
    c: Horizontal(g97)
    c: Equal(g94,g11)
    c: Equal(g11,g12)
    c: Equal(g12,g95)
    c: Equal(g23,g16)
    c: Equal(g20,g16)
    c: PointOnObject(g98,g7)
    c: PointOnObject(g99,g7)
    c: PointOnObject(g100,g7)
    c: PointOnObject(g101,g7)
    c: PointOnObject(g102,g7)
    c: Equal(g98,g99)
    c: Equal(g99,g100)
    c: Equal(g100,g101)
    c: Equal(g101,g102)
    c: DistanceX(g99,g100) = 40
    c: DistanceX(g100,g101) = 40
    c: DistanceX(g101,g102) = 40
    c: DistanceX(g98,g6) = 457
    c: DistanceX(g6,g102) = 65
    c: Horizontal(g103)
    c: Coincident(g104,g103)
    c: Horizontal(g104)
    c: Coincident(g105,g104)
    c: Coincident(g105,g26)
    c: Horizontal(g105)
    c: Coincident(g106,g26)
    c: Coincident(g106,g74)
    c: Horizontal(g106)
    c: Coincident(g107,g74)
    c: Coincident(g107,g25)
    c: Horizontal(g107)
    c: Coincident(g108,g25)
    c: Horizontal(g108)
    c: Coincident(g109,g108)
    c: Horizontal(g109)
    c: Coincident(g110,g109)
    c: Horizontal(g110)
    c: Symmetric(g71,g69,g109)
    c: Symmetric(g70,g68,g108)
    c: Symmetric(g21,g22,g25)
    c: Symmetric(g19,g20,g74)
    c: Symmetric(g18,g17,g26)
    c: Symmetric(g89,g91,g104)
    c: Symmetric(g88,g90,g103)
    c: Vertical(g9)
    c: Vertical(g67)
    c: Vertical(g66)
    c: Vertical(g10)
    c: Vertical(g8)
    c: Vertical(g86)
    c: Vertical(g87)
    c: Equal(g103,g104)
    c: Equal(g110,g109)
    c: Horizontal(g111)
    c: Horizontal(g113)
    c: Vertical(g112)
    c: Vertical(g114)
    c: Vertical(g117)
    c: PointOnObject(g118,g116)
    c: Horizontal(g118)
    c: Vertical(g119)
    c: PointOnObject(g120,g115)
    c: Horizontal(g120)
    c: Coincident(g121,g120)
    c: Vertical(g121)
    c: Coincident(g122,g117)
    c: Horizontal(g122)
    c: Coincident(g123,g118)
    c: Vertical(g123)
    c: Coincident(g124,g119)
    c: Horizontal(g124)
    c: Equal(g121,g120)
    c: Equal(g124,g119)
    c: Equal(g123,g118)
    c: Equal(g121,g117)
    c: Tangent(g115,g125) = 1.5708
    c: Tangent(g114,g125) = -1.5708
    c: Tangent(g115,g126) = 1.5708
    c: Tangent(g111,g126) = -1.5708
    c: Tangent(g113,g127) = -1.5708
    c: Tangent(g116,g127) = 1.5708
    c: Tangent(g116,g128) = 1.5708
    c: Tangent(g112,g128) = -1.5708
    c: Equal(g128,g116)
    c: Equal(g116,g127)
    c: Coincident(g113,g118)
    c: Coincident(g112,g123)
    c: Coincident(g114,g121)
    c: Coincident(g111,g120)
    c: Equal(g126,g115)
    c: Equal(g125,g115)
    c: Equal(g122,g117)
    c: PointOnObject(g119,g129)
    c: Tangent(g129,g130) = 1.5708
    c: Tangent(g111,g130) = -1.5708
    c: Tangent(g129,g131) = 1.5708
    c: Tangent(g112,g131) = -1.5708
    c: Coincident(g111,g124)
    c: Coincident(g119,g112)
    c: Equal(g130,g129)
    c: Equal(g129,g131)
    c: PointOnObject(g117,g132)
    c: Tangent(g114,g133) = -1.5708
    c: Tangent(g132,g133) = 1.5708
    c: Coincident(g117,g114)
    c: Tangent(g132,g134) = 1.5708
    c: Tangent(g113,g134) = -1.5708
    c: Coincident(g122,g113)
    c: Equal(g133,g132)
    c: Equal(g132,g134)
    c: Equal(g129,g116)
    c: Equal(g132,g129)
    c: DistanceX(g117,g118) = 13.2
    c: Symmetric(g81,g84,g135)
    c: Symmetric(g117,g119,g135)
    c: PointOnObject(g136,g1)
    c: Horizontal(g136)
    c: Coincident(g137,g76)
    c: Equal(g137,g136)
    c: DistanceX(g136,g136) = 35
    c: DistanceX(g103,g103) = 50
    c: DistanceY(g136,g-1) = 50
    c: Symmetric(g136,g137,g-2)
    c: Equal(g109,g103)
    c: DistanceX(g1,g64) = 320
    c: Horizontal(g76)
    c: Distance(g135,g83) = 26.4197
    c: DistanceY(g117,g120) = 12.4
    c: Radius(g115) = 2
    c: DistanceY(g68,g84) = 101
    c: DistanceX(g5,g22) = 247.282
    c: DistanceY(g16,g-1) = 26
    c: Vertical(g138)
    c: Symmetric(g138,g76,g77)
    c: DistanceX(g23,g84) = 27
    c: Coincident(g139,g27)
    c: Horizontal(g139)
    c: Coincident(g140,g5)
    c: Equal(g2,g140)
    c: Symmetric(g24,g23,g110)
    c: Coincident(g110,g137)
    c: PointOnObject(g143,g138)
    c: PointOnObject(g143,g61)
    c: Horizontal(g143)
    c: DistanceY(g76,g143) = 10
    c: Coincident(g144,g141)
    c: Coincident(g145,g142)
    c: Equal(g145,g144)
    c: Equal(g144,g77)
    c: Coincident(g146,g144)
    c: Vertical(g146)
    c: Coincident(g147,g144)
    c: Coincident(g147,g145)
    c: Vertical(g147)
    c: Coincident(g148,g145)
    c: PointOnObject(g148,g32)
    c: Vertical(g148)
    c: Symmetric(g143,g143,g146)
    c: PointOnObject(g149,g27)
    c: Vertical(g149)
    c: Coincident(g150,g149)
    c: PointOnObject(g150,g1)
    c: Horizontal(g150)
    c: DistanceY(g136,g150) = 10
    c: PointOnObject(g151,g136)
    c: Vertical(g152)
    c: Coincident(g153,g152)
    c: Vertical(g153)
    c: Coincident(g154,g153)
    c: PointOnObject(g154,g27)
    c: Vertical(g154)
    c: Coincident(g155,g152)
    c: Coincident(g156,g153)
    c: DistanceX(g136,g151) = 10
    c: Coincident(g103,g136)
    c: Symmetric(g150,g149,g152)
    c: Equal(g156,g26)
    c: Equal(g26,g74)
    c: Equal(g74,g25)
    c: Equal(g25,g77)
    c: Equal(g34,g86)
    c: PointOnObject(g103,g34)
    c: Equal(g65,g151)
    c: Coincident(g160,g157)
    c: PointOnObject(g160,g95)
    c: Vertical(g160)
    c: Coincident(g161,g158)
    c: PointOnObject(g161,g95)
    c: Vertical(g161)
    c: Coincident(g162,g159)
    c: PointOnObject(g162,g95)
    c: Vertical(g162)
    c: Equal(g34,g160)
    c: Equal(g160,g161)
    c: Equal(g161,g162)
    c: Equal(g157,g158)
    c: Equal(g158,g159)
    c: Equal(g159,g16)
    c: Equal(g163,g151)
    c: Coincident(g164,g163)
    c: Vertical(g164)
    c: DistanceY(g-1,g164) = 10
    c: Coincident(g165,g164)
    c: Equal(g163,g165)
    c: DistanceY(g-1,g155) = 10
    c: DistanceY(g-1,g144) = 10
    c: PointOnObject(g1,g85)
    c: PointOnObject(g1,g27)
    c: DistanceX(g1,g27) = 338
    c: Vertical(g166)
    c: Tangent(g27,g167) = 1.5708
    c: Tangent(g166,g167) = -1.5708
    c: Tangent(g166,g168) = -1.5708
    c: Tangent(g85,g168) = 1.5708
    c: DistanceY(g-1,g27) = 140
    c: Equal(g167,g168)
    c: Equal(g169,g170)
    c: Tangent(g32,g171) = 1.5708
    c: Tangent(g4,g171) = 1.5708
    c: Coincident(g139,g32)
    c: Radius(g171) = 12
    c: Radius(g72) = 4
    c: Equal(g167,g72)
    c: PointOnObject(g172,g153)
    c: DistanceY(g155,g172) = 20
    c: Equal(g172,g151)
    c: DistanceY(g154,g154) = 10
    c: Equal(g154,g148)
    c: DistanceY(g64,g27) = 10
    c: DistanceY(g169,g170) = 188
    c: Equal(g173,g170)
    c: Symmetric(g170,g169,g173)
    c: DistanceY(g148,g148) = 10
    c: Coincident(g174,g169)
    c: PointOnObject(g174,g85)
    c: Vertical(g174)
    c: Coincident(g175,g169)
    c: Coincident(g175,g173)
    c: Vertical(g175)
    c: Coincident(g176,g173)
    c: Coincident(g176,g170)
    c: Coincident(g177,g170)
    c: PointOnObject(g177,g27)
    c: Vertical(g177)
    c: Coincident(g178,g35)
    c: Coincident(g178,g169)
    c: Equal(g174,g177)
    c: Horizontal(g178)
    c: DistanceX(g166,g174) = 20
    c: DistanceX(g174,g1) = 20
    c: DistanceX(g1,g149) = 20
    c: DistanceX(g4,g44) = 55
    c: DistanceX(g44,g46) = 25.3
    c: DistanceX(g46,g81) = 40.7
    c: DistanceX(g81,g82) = 23
    c: PointOnObject(g138,g32)
    c: DistanceX(g82,g138) = 15
    c: DistanceX(g1,g163) = 908
    c: DistanceX(g64,g179) = 25
    c: DistanceX(g179,g163) = 563
    c: DistanceX(g110,g76) = 35
    c: DistanceX(g78,g84) = 166
    c: DistanceY(g78,g84) = 30
    c: DistanceX(g180,g37) = 12.5
    c: Equal(g180,g83)
    c: DistanceY(g180,g60) = 70
    c: DistanceX(g21,g160) = 80
    c: DistanceX(g160,g161) = 80
    c: DistanceX(g161,g162) = 80
    c: DistanceY(g179,g27) = 15
    c: DistanceY(g74,g179) = 175
    c: Vertical(g181)
    c: Tangent(g181,g33) = 1.5708
    c: Tangent(g182,g181) = -1.5708
    c: Tangent(g182,g3) = -1.5708
    c: DistanceX(g102,g33) = 52.782
    c: DistanceX(g102,g33) = 32.782
    c: DistanceX(g65,g98) = 33.218
    c: PointOnObject(g183,g108)
    c: DistanceX(g22,g183) = 12.5
    c: DistanceX(g183,g39) = 356
    c: Coincident(g184,g2)
    c: Vertical(g184)
    c: Coincident(g185,g2)
    c: Coincident(g185,g2)
    c: Coincident(g2,g184)
    c: Coincident(g186,g2)
    c: Coincident(g186,g2)
    c: Coincident(g186,g2)
    c: Vertical(g185)
    c: Equal(g172,g156)
    c: Horizontal(g187)
    c: Coincident(g188,g187)
    c: Coincident(g189,g187)
    c: Symmetric(g187,g187,g190)
    c: DistanceX(g190,g5) = 300.5
    c: DistanceX(g187,g187) = 50
    c: DistanceY(g100,g189) = 17.8
    c: Equal(g188,g189)
    c: PointOnObject(g7,g181)
    c: Radius(g182) = 45
    c: Radius(g33) = 20
    c: Diameter(g83) = 13
    c: Coincident(g191,g108)
    c: Coincident(g192,g104)
    c: Equal(g151,g192)
    c: Equal(g192,g191)
    c: DistanceY(g19,g165) = 84
    c: DistanceX(g19,g165) = 158
    c: Diameter(g2) = 30
    c: Coincident(g193,g2)
    c: Diameter(g193) = 13
    c: Coincident(g194,g188)
    c: Coincident(g194,g65)
    c: Horizontal(g194)
    c: Coincident(g195,g5)
    c: Diameter(g195) = 45
    c: DistanceY(g188,g29) = 6
    c: DistanceY(g165,g163) = 52
    c: Diameter(g98) = 9
    c: Diameter(g189) = 7
    c: Diameter(g170) = 13
    c: Diameter(g156) = 6
    c: Diameter(g155) = 7
    c: Diameter(g15) = 13
    c: Diameter(g179) = 9
    c: Equal(g16,g170)
    c: DistanceX(g5,g39) = 615.782
FEATURE [PartDesign::Pad] Pad  label="Plate thickness"
  Direction = (1,1,1)
  Length = 8
  Length2 = 100
  Profile = -> Sketch
  Type = 0
FEATURE [PartDesign::Body] Body
  Group = -> [Sketch,Pad]
  Origin = -> Origin
  Tip = -> Pad
